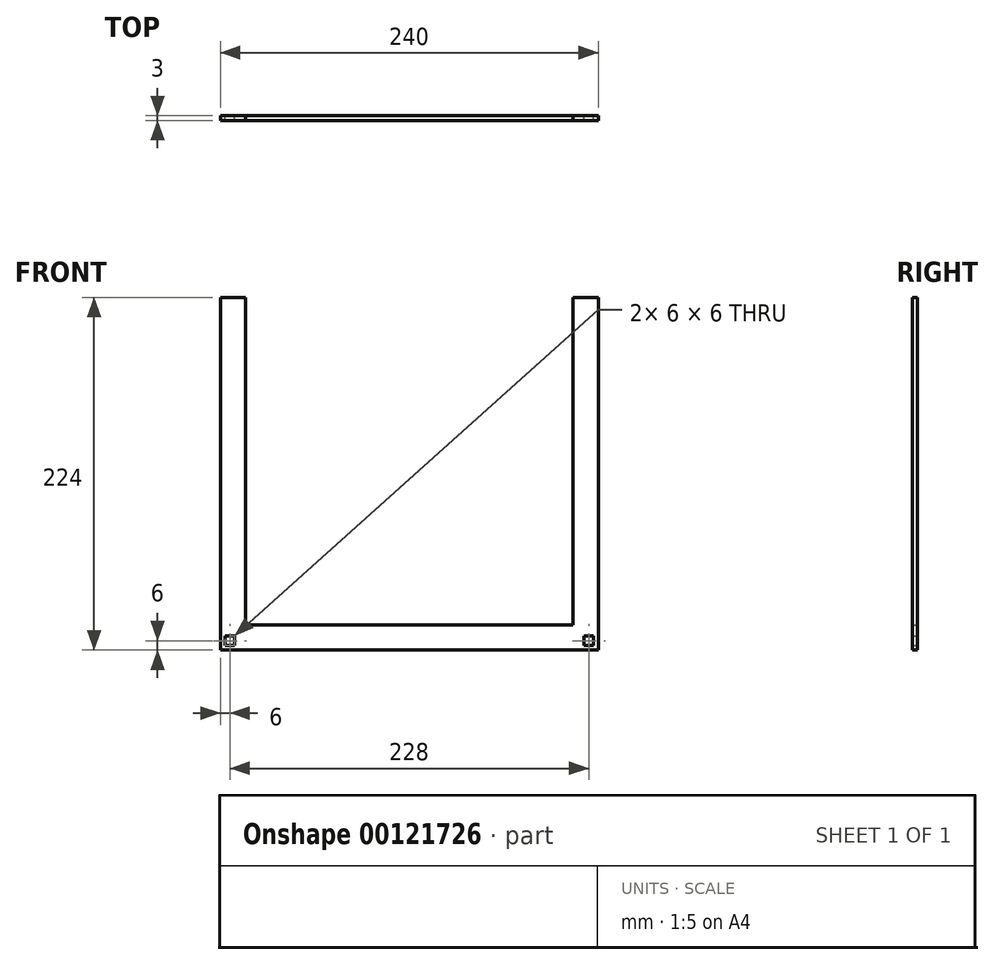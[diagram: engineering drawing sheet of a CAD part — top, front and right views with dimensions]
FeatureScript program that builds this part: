
annotation { "Feature Type Name" : "Feature", "Feature Type Description" : "" }
export const myFeature = defineFeature(function(context is Context, id is Id, definition is map)
    precondition{}
    {
        {
            assignVariable(context, id + "F0", {"name" : "thicknessWood", "anyValue" : 3});
        }
        {
            var Q0;
            Q0=qCreatedBy(makeId("Front.planeOp"),FACE);
            var sketch = newSketch(context, id + "F1", { "sketchPlane" : qUnion([Q0])});
            skLineSegment(sketch, "E0.bottom", {"start": v(0, 0) * mm, "end": v(240, 0) * mm});
            skLineSegment(sketch, "E0.top", {"start": v(0, 240) * mm, "end": v(240, 240) * mm});
            skLineSegment(sketch, "E0.left", {"start": v(0, 0) * mm, "end": v(0, 240) * mm});
            skLineSegment(sketch, "E0.right", {"start": v(240, 0) * mm, "end": v(240, 240) * mm});
            skLineSegment(sketch, "E1.bottom", {"start": v(16, 224) * mm, "end": v(224, 224) * mm});
            skLineSegment(sketch, "E1.top", {"start": v(16, 16) * mm, "end": v(224, 16) * mm});
            skLineSegment(sketch, "E1.left", {"start": v(16, 224) * mm, "end": v(16, 16) * mm});
            skLineSegment(sketch, "E1.right", {"start": v(224, 224) * mm, "end": v(224, 16) * mm});
            skLineSegment(sketch, "E2.bottom", {"start": v(9, 237) * mm, "end": v(3, 237) * mm});
            skLineSegment(sketch, "E2.top", {"start": v(9, 231) * mm, "end": v(3, 231) * mm});
            skLineSegment(sketch, "E2.left", {"start": v(9, 237) * mm, "end": v(9, 231) * mm});
            skLineSegment(sketch, "E2.right", {"start": v(3, 237) * mm, "end": v(3, 231) * mm});
            skLineSegment(sketch, "E3", {"start": v(120, 240) * mm, "end": v(120, 0) * mm, "construction": true});
            skLineSegment(sketch, "E4", {"start": v(0, 120) * mm, "end": v(240, 120) * mm, "construction": true});
            skSolve(sketch);
        }
        {
            var Q0;
            Q0=makeQuery(id+"F1.imprint","IMPRINT",FACE,{"disambiguationData":[TD([[makeQuery(id+"F1.imprint","IMPRINT",EDGE,{"derivedFrom":sQuery(id+"F1.wireOp",EDGE,"E0.bottom")}),1.0]])]});
            var Q1;
            Q1=makeQuery(id+"F1.imprint","IMPRINT",FACE,{"disambiguationData":[TD([[makeQuery(id+"F1.imprint","IMPRINT",EDGE,{"derivedFrom":sQuery(id+"F1.wireOp",EDGE,"E2.bottom")}),1.0]])]});
            var Q2;
            Q2=sQuery(id+"F1.wireOp",EDGE,"E1.left");
            extrude(context, id + "F2", {"entities" : qUnion([Q0, Q1]), "surfaceEntities" : qUnion([Q2]), "depth" : (getVariable(context, 'thicknessWood')) * mm});
        }
        {
            var Q0;
            Q0=makeQuery(id+"F1.imprint","IMPRINT",FACE,{"disambiguationData":[TD([[makeQuery(id+"F1.imprint","IMPRINT",EDGE,{"derivedFrom":sQuery(id+"F1.wireOp",EDGE,"E2.bottom")}),1.0]])]});
            extrude(context, id + "F3", {"entities" : qUnion([Q0]), "operationType" : NewBodyOperationType.REMOVE, "depth" : 25 * mm});
        }
        {
            var Q0;
            Q0=makeQuery(id+"F2.opExtrude","SWEPT_FACE",FACE,{"disambiguationData":[OSD([sQuery(id+"F1.wireOp",EDGE,"E0.left")])]});
            var Q1;
            Q1=makeQuery(id+"F2.opExtrude","SWEPT_FACE",FACE,{"disambiguationData":[OSD([sQuery(id+"F1.wireOp",EDGE,"E0.right")])]});
            cPlane(context, id + "F4", {"entities" : qUnion([Q0, Q1]), "cplaneType" : CPlaneType.MID_PLANE, "offset" : 25 * mm, "width" : 150 * mm, "height" : 150 * mm});
        }
        {
            var Q0;
            Q0=makeQuery(id+"F2.opExtrude","SWEPT_BODY",BODY,{"disambiguationData":[OSD([sQuery(id+"F1.wireOp",EDGE,"E0.bottom"),sQuery(id+"F1.wireOp",EDGE,"E0.top"),sQuery(id+"F1.wireOp",EDGE,"E0.left"),sQuery(id+"F1.wireOp",EDGE,"E0.right"),sQuery(id+"F1.wireOp",EDGE,"E1.bottom"),sQuery(id+"F1.wireOp",EDGE,"E1.top"),sQuery(id+"F1.wireOp",EDGE,"E1.left"),sQuery(id+"F1.wireOp",EDGE,"E1.right")])]});
            var Q1;
            Q1=qCreatedBy(id+"F4.planeOp",FACE);
            mirror(context, id + "F5", {"operationType" : NewBodyOperationType.INTERSECT, "entities" : qUnion([Q0]), "mirrorPlane" : qUnion([Q1])});
        }
        {
            var Q0;
            Q0=makeQuery(id+"F2.opExtrude","SWEPT_FACE",FACE,{"disambiguationData":[OSD([sQuery(id+"F1.wireOp",EDGE,"E0.top")])]});
            var Q1;
            Q1=makeQuery(id+"F2.opExtrude","SWEPT_FACE",FACE,{"disambiguationData":[OSD([sQuery(id+"F1.wireOp",EDGE,"E0.bottom")])]});
            cPlane(context, id + "F6", {"entities" : qUnion([Q0, Q1]), "cplaneType" : CPlaneType.MID_PLANE, "offset" : 25 * mm, "width" : 150 * mm, "height" : 150 * mm});
        }
        {
            var Q0;
            Q0=makeQuery(id+"F2.opExtrude","SWEPT_BODY",BODY,{"disambiguationData":[OSD([sQuery(id+"F1.wireOp",EDGE,"E0.bottom"),sQuery(id+"F1.wireOp",EDGE,"E0.top"),sQuery(id+"F1.wireOp",EDGE,"E0.left"),sQuery(id+"F1.wireOp",EDGE,"E0.right"),sQuery(id+"F1.wireOp",EDGE,"E1.bottom"),sQuery(id+"F1.wireOp",EDGE,"E1.top"),sQuery(id+"F1.wireOp",EDGE,"E1.left"),sQuery(id+"F1.wireOp",EDGE,"E1.right")])]});
            var Q1;
            Q1=qCreatedBy(id+"F6.planeOp",FACE);
            mirror(context, id + "F7", {"operationType" : NewBodyOperationType.INTERSECT, "entities" : qUnion([Q0]), "mirrorPlane" : qUnion([Q1])});
        }
        {
            var Q0;
            Q0=makeQuery(id+"F2.opExtrude","CAP_FACE",FACE,{"disambiguationData":[OSD([sQuery(id+"F1.wireOp",EDGE,"E0.bottom"),sQuery(id+"F1.wireOp",EDGE,"E0.top"),sQuery(id+"F1.wireOp",EDGE,"E0.left"),sQuery(id+"F1.wireOp",EDGE,"E0.right"),sQuery(id+"F1.wireOp",EDGE,"E1.bottom"),sQuery(id+"F1.wireOp",EDGE,"E1.top"),sQuery(id+"F1.wireOp",EDGE,"E1.left"),sQuery(id+"F1.wireOp",EDGE,"E1.right")])],"isStart":false});
            var sketch = newSketch(context, id + "F8", { "sketchPlane" : qUnion([Q0])});
            skLineSegment(sketch, "E5.bottom", {"start": v(0, 240) * mm, "end": v(240, 240) * mm});
            skLineSegment(sketch, "E5.top", {"start": v(0, 224) * mm, "end": v(240, 224) * mm});
            skLineSegment(sketch, "E5.left", {"start": v(0, 240) * mm, "end": v(0, 224) * mm});
            skLineSegment(sketch, "E5.right", {"start": v(240, 240) * mm, "end": v(240, 224) * mm});
            skLineSegment(sketch, "E6.bottom", {"start": v(240, 224) * mm, "end": v(224, 224) * mm});
            skLineSegment(sketch, "E6.top", {"start": v(240, 16) * mm, "end": v(224, 16) * mm});
            skLineSegment(sketch, "E6.left", {"start": v(240, 224) * mm, "end": v(240, 16) * mm});
            skLineSegment(sketch, "E6.right", {"start": v(224, 224) * mm, "end": v(224, 16) * mm});
            skSolve(sketch);
        }
        {
            var Q0;
            Q0=makeQuery(id+"F8.imprint","IMPRINT",FACE,{"disambiguationData":[TD([[makeQuery(id+"F8.imprint","IMPRINT",EDGE,{"derivedFrom":sQuery(id+"F8.wireOp",EDGE,"E5.bottom")}),-1.0]])]});
            var Q1;
            Q1=makeQuery(id+"F8.imprint","IMPRINT",FACE,{"disambiguationData":[TD([[makeQuery(id+"F8.imprint","IMPRINT",EDGE,{"derivedFrom":sQuery(id+"F8.wireOp",EDGE,"E6.bottom")}),1.0]])]});
            extrude(context, id + "F9", {"entities" : qUnion([Q0, Q1]), "operationType" : NewBodyOperationType.REMOVE, "endBound" : BoundingType.THROUGH_ALL, "oppositeDirection" : true, "depth" : 25 * mm});
        }
    });
